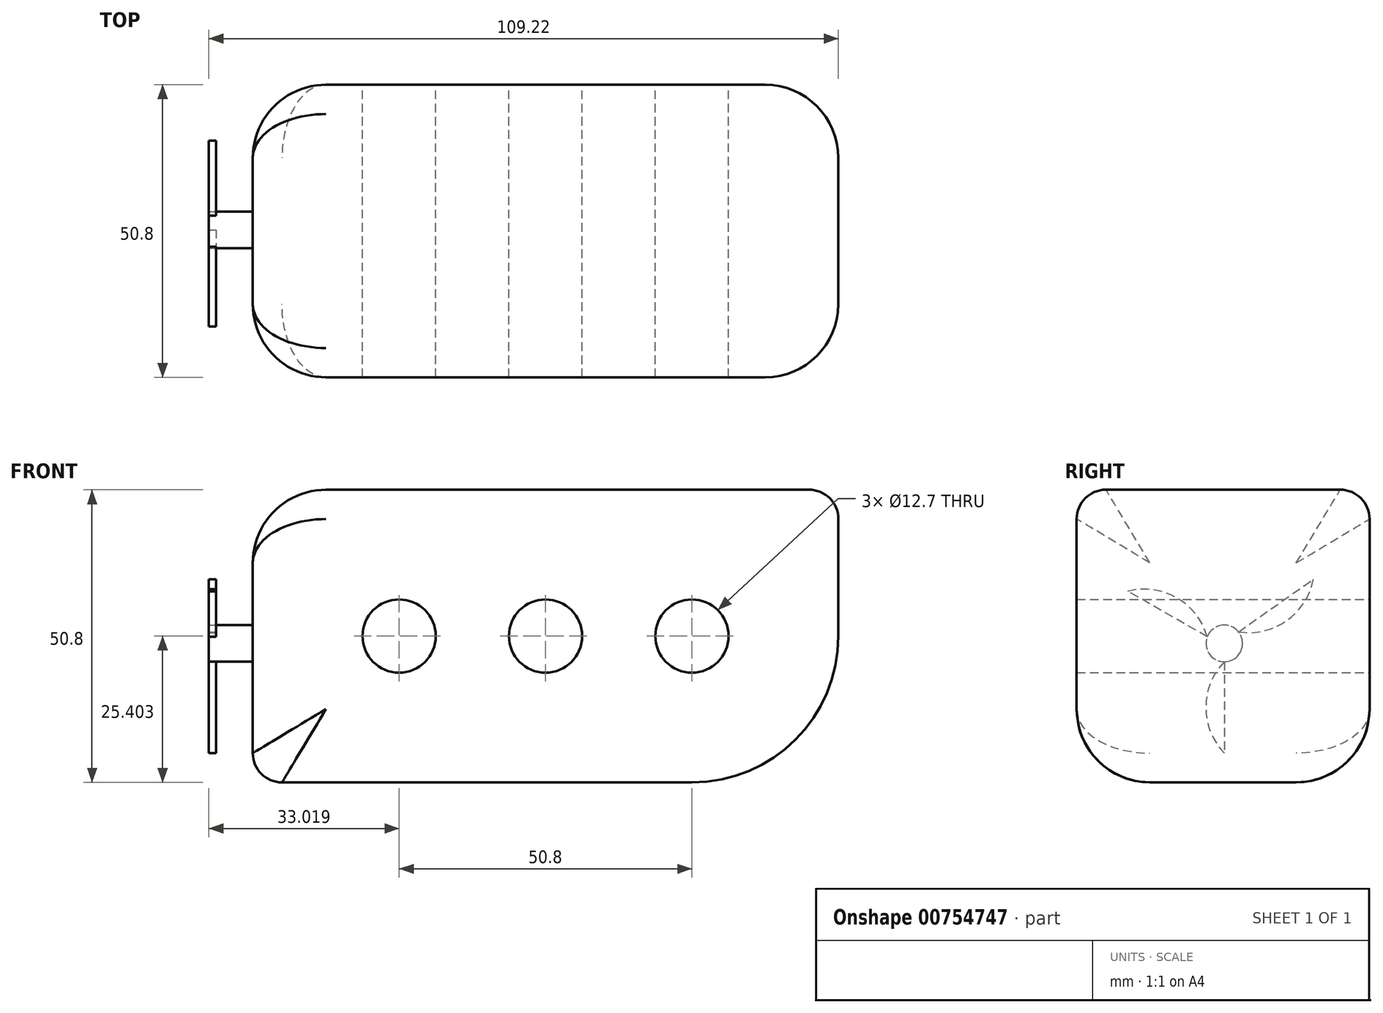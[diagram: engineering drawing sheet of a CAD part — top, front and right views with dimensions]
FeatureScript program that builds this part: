
annotation { "Feature Type Name" : "Feature", "Feature Type Description" : "" }
export const myFeature = defineFeature(function(context is Context, id is Id, definition is map)
    precondition{}
    {
        {
            var Q0;
            Q0=qCreatedBy(makeId("Front.planeOp"),FACE);
            var sketch = newSketch(context, id + "F0", { "sketchPlane" : qUnion([Q0])});
            skLineSegment(sketch, "E0.bottom", {"start": v(-59.1, 31.1) * mm, "end": v(42.5, 31.1) * mm});
            skLineSegment(sketch, "E0.top", {"start": v(-59.1, -19.7) * mm, "end": v(42.5, -19.7) * mm});
            skLineSegment(sketch, "E0.left", {"start": v(-59.1, 31.1) * mm, "end": v(-59.1, -19.7) * mm});
            skLineSegment(sketch, "E0.right", {"start": v(42.5, 31.1) * mm, "end": v(42.5, -19.7) * mm});
            skCircle(sketch, "E1", {"center": v(-8.3, 5.7) * mm, "radius": 6.35 * mm});
            skCircle(sketch, "E2", {"center": v(-33.7, 5.7) * mm, "radius": 6.35 * mm});
            skCircle(sketch, "E3", {"center": v(17.1, 5.7) * mm, "radius": 6.35 * mm});
            skSolve(sketch);
        }
        {
            var Q0;
            Q0 = qSketchRegion(id + "F0", true);
            extrude(context, id + "F1", {"entities" : qUnion([Q0]), "depth" : 50.8 * mm, "offsetDistance" : 25.4 * mm});
        }
        {
            var Q0;
            Q0=makeQuery(id+"F1.opExtrude","SWEPT_EDGE",EDGE,{"disambiguationData":[OSD([sQuery(id+"F0.wireOp",EDGE,"E0.top"),sQuery(id+"F0.wireOp",EDGE,"E0.right")])]});
            fillet(context, id + "F2", {"entities" : qUnion([Q0]), "radius" : 25.4 * mm, "tangentPropagation" : true, "allowEdgeOverflow" : false});
        }
        {
            var Q0;
            Q0=makeQuery(id+"F1.opExtrude","CAP_EDGE",EDGE,{"disambiguationData":[OSD([sQuery(id+"F0.wireOp",EDGE,"E0.top")])],"isStart":false});
            var Q1;
            {var subQ0=sQuery(id+"F0.wireOp",EDGE,"E0.right");var subQ1=sQuery(id+"F0.wireOp",EDGE,"E0.top");Q1=makeQuery(id+"F2.opFillet","BLEND_EDGE",EDGE,{"blendedFrom":[makeQuery(id+"F1.opExtrude","SWEPT_EDGE",EDGE,{"disambiguationData":[OSD([subQ1,subQ0])]}),makeQuery(id+"F1.opExtrude","CAP_FACE",FACE,{"disambiguationData":[OSD([sQuery(id+"F0.wireOp",EDGE,"E0.bottom"),subQ1,sQuery(id+"F0.wireOp",EDGE,"E0.left"),subQ0,sQuery(id+"F0.wireOp",EDGE,"E1"),sQuery(id+"F0.wireOp",EDGE,"E2"),sQuery(id+"F0.wireOp",EDGE,"E3")])],"isStart":true})],"blendedInto":[makeQuery(id+"F1.opExtrude","CAP_FACE",FACE,{"disambiguationData":[OSD([sQuery(id+"F0.wireOp",EDGE,"E0.bottom"),subQ1,sQuery(id+"F0.wireOp",EDGE,"E0.left"),subQ0,sQuery(id+"F0.wireOp",EDGE,"E1"),sQuery(id+"F0.wireOp",EDGE,"E2"),sQuery(id+"F0.wireOp",EDGE,"E3")])],"isStart":true})]});}
            var Q2;
            Q2=makeQuery(id+"F1.opExtrude","CAP_EDGE",EDGE,{"disambiguationData":[OSD([sQuery(id+"F0.wireOp",EDGE,"E0.left")])],"isStart":false});
            var Q3;
            Q3=makeQuery(id+"F1.opExtrude","CAP_EDGE",EDGE,{"disambiguationData":[OSD([sQuery(id+"F0.wireOp",EDGE,"E0.left")])],"isStart":true});
            var Q4;
            Q4=makeQuery(id+"F1.opExtrude","SWEPT_EDGE",EDGE,{"disambiguationData":[OSD([sQuery(id+"F0.wireOp",EDGE,"E0.bottom"),sQuery(id+"F0.wireOp",EDGE,"E0.left")])]});
            fillet(context, id + "F3", {"entities" : qUnion([Q0, Q1, Q2, Q3, Q4]), "radius" : 12.7 * mm, "tangentPropagation" : true, "allowEdgeOverflow" : false});
        }
        {
            var Q0;
            Q0=makeQuery(id+"F1.opExtrude","CAP_EDGE",EDGE,{"disambiguationData":[OSD([sQuery(id+"F0.wireOp",EDGE,"E0.bottom")])],"isStart":true});
            var Q1;
            Q1=makeQuery(id+"F1.opExtrude","CAP_EDGE",EDGE,{"disambiguationData":[OSD([sQuery(id+"F0.wireOp",EDGE,"E0.bottom")])],"isStart":false});
            fillet(context, id + "F4", {"entities" : qUnion([Q0, Q1]), "radius" : 5.08 * mm, "tangentPropagation" : true, "allowEdgeOverflow" : false});
        }
        {
            var Q0;
            Q0=makeQuery(id+"F1.opExtrude","SWEPT_EDGE",EDGE,{"disambiguationData":[OSD([sQuery(id+"F0.wireOp",EDGE,"E0.top"),sQuery(id+"F0.wireOp",EDGE,"E0.left")])]});
            fillet(context, id + "F5", {"entities" : qUnion([Q0]), "radius" : 5.08 * mm, "tangentPropagation" : true, "allowEdgeOverflow" : false});
        }
        {
            var Q0;
            Q0=makeQuery(id+"F1.opExtrude","SWEPT_FACE",FACE,{"disambiguationData":[OSD([sQuery(id+"F0.wireOp",EDGE,"E0.left")])]});
            var sketch = newSketch(context, id + "F6", { "sketchPlane" : qUnion([Q0])});
            skCircle(sketch, "E4", {"center": v(25.2, 4.43) * mm, "radius": 3.18 * mm});
            skSolve(sketch);
        }
        {
            var Q0;
            Q0 = qSketchRegion(id + "F6", true);
            extrude(context, id + "F7", {"entities" : qUnion([Q0]), "operationType" : NewBodyOperationType.ADD, "depth" : 6.35 * mm, "offsetDistance" : 25.4 * mm});
        }
        {
            var Q0;
            Q0=makeQuery(id+"F7.opExtrude","CAP_FACE",FACE,{"disambiguationData":[OSD([sQuery(id+"F6.wireOp",EDGE,"E4")])],"isStart":false});
            var sketch = newSketch(context, id + "F8", { "sketchPlane" : qUnion([Q0])});
            skCircle(sketch, "E5", {"center": v(25.2, 4.43) * mm, "radius": 19.05 * mm});
            skLineSegment(sketch, "E6", {"start": v(25.2, 1.25) * mm, "end": v(25.2, -14.62) * mm});
            skLineSegment(sketch, "E7", {"start": v(22.73, 6.43) * mm, "end": v(9.74, 15.56) * mm});
            skLineSegment(sketch, "E8", {"start": v(28.14, 5.6) * mm, "end": v(41.95, 13.49) * mm});
            skArc(sketch, "E9", {"start": v(9.74, 15.56) * mm, "mid": v(14.4, 8.37) * mm, "end": v(22.73, 6.43) * mm});
            skArc(sketch, "E10", {"start": v(41.95, 13.49) * mm, "mid": v(33.45, 12.34) * mm, "end": v(28.14, 5.6) * mm});
            skArc(sketch, "E11", {"start": v(25.2, -14.62) * mm, "mid": v(28.4, -6.68) * mm, "end": v(25.2, 1.25) * mm});
            skSolve(sketch);
        }
        {
            var Q0;
            Q0=makeQuery(id+"F8.imprint","IMPRINT",FACE,{"disambiguationData":[TD([[makeQuery(id+"F8.imprint","IMPRINT",EDGE,{"derivedFrom":sQuery(id+"F8.wireOp",EDGE,"E6")}),1.0]])]});
            var Q1;
            Q1=makeQuery(id+"F8.imprint","IMPRINT",FACE,{"disambiguationData":[TD([[makeQuery(id+"F8.imprint","IMPRINT",EDGE,{"derivedFrom":sQuery(id+"F8.wireOp",EDGE,"E8")}),1.0]])]});
            var Q2;
            Q2=makeQuery(id+"F8.imprint","IMPRINT",FACE,{"disambiguationData":[TD([[makeQuery(id+"F8.imprint","IMPRINT",EDGE,{"derivedFrom":sQuery(id+"F8.wireOp",EDGE,"E7")}),1.0]])]});
            var Q3;
            {var subQ0=makeQuery(id+"F7.opExtrude","CAP_EDGE",EDGE,{"disambiguationData":[OSD([sQuery(id+"F6.wireOp",EDGE,"E4")])],"isStart":false});var subQ1=makeQuery(id+"F8.imprint","INTERSECT",VERTEX,{"derivedFrom":[subQ0,sQuery(id+"F8.wireOp",EDGE,"E6"),sQuery(id+"F8.wireOp",EDGE,"E11")]});Q3=makeQuery(id+"F8.imprint","IMPRINT",FACE,{"disambiguationData":[TD([[makeQuery(id+"F8.imprint","IMPRINT",EDGE,{"disambiguationData":[TD([[subQ1,1.0]])],"derivedFrom":subQ0}),1.0]])]});}
            extrude(context, id + "F9", {"entities" : qUnion([Q0, Q1, Q2, Q3]), "operationType" : NewBodyOperationType.ADD, "depth" : 1.27 * mm, "offsetDistance" : 25.4 * mm});
        }
    });
